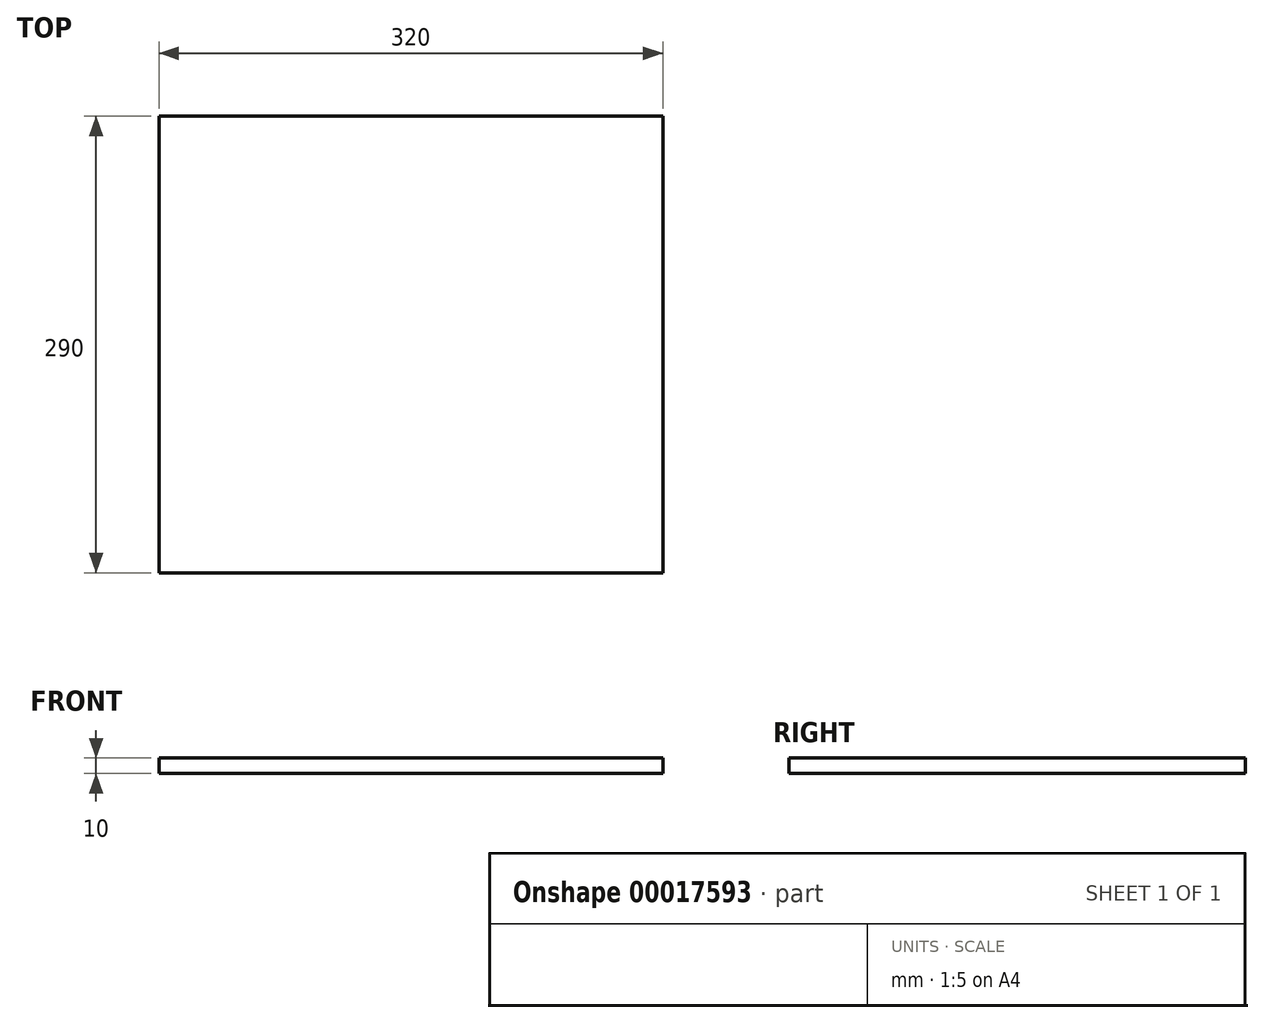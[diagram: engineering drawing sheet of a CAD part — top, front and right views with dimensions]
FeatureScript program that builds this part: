
annotation { "Feature Type Name" : "Feature", "Feature Type Description" : "" }
export const myFeature = defineFeature(function(context is Context, id is Id, definition is map)
    precondition{}
    {
        {
            var Q0;
            Q0=qCreatedBy(makeId("Top.planeOp"),FACE);
            var sketch = newSketch(context, id + "F0", { "sketchPlane" : qUnion([Q0])});
            skLineSegment(sketch, "E0.bottom", {"start": v(-70.96, 65.05) * mm, "end": v(249.04, 65.05) * mm});
            skLineSegment(sketch, "E0.top", {"start": v(-70.96, -224.95) * mm, "end": v(249.04, -224.95) * mm});
            skLineSegment(sketch, "E0.left", {"start": v(-70.96, 65.05) * mm, "end": v(-70.96, -224.95) * mm});
            skLineSegment(sketch, "E0.right", {"start": v(249.04, 65.05) * mm, "end": v(249.04, -224.95) * mm});
            skSolve(sketch);
        }
        {
            var Q0;
            Q0=qSketchRegion(id+"F0",true);
            extrude(context, id + "F1", {"entities" : qUnion([Q0]), "depth" : 10 * mm});
        }
    });
